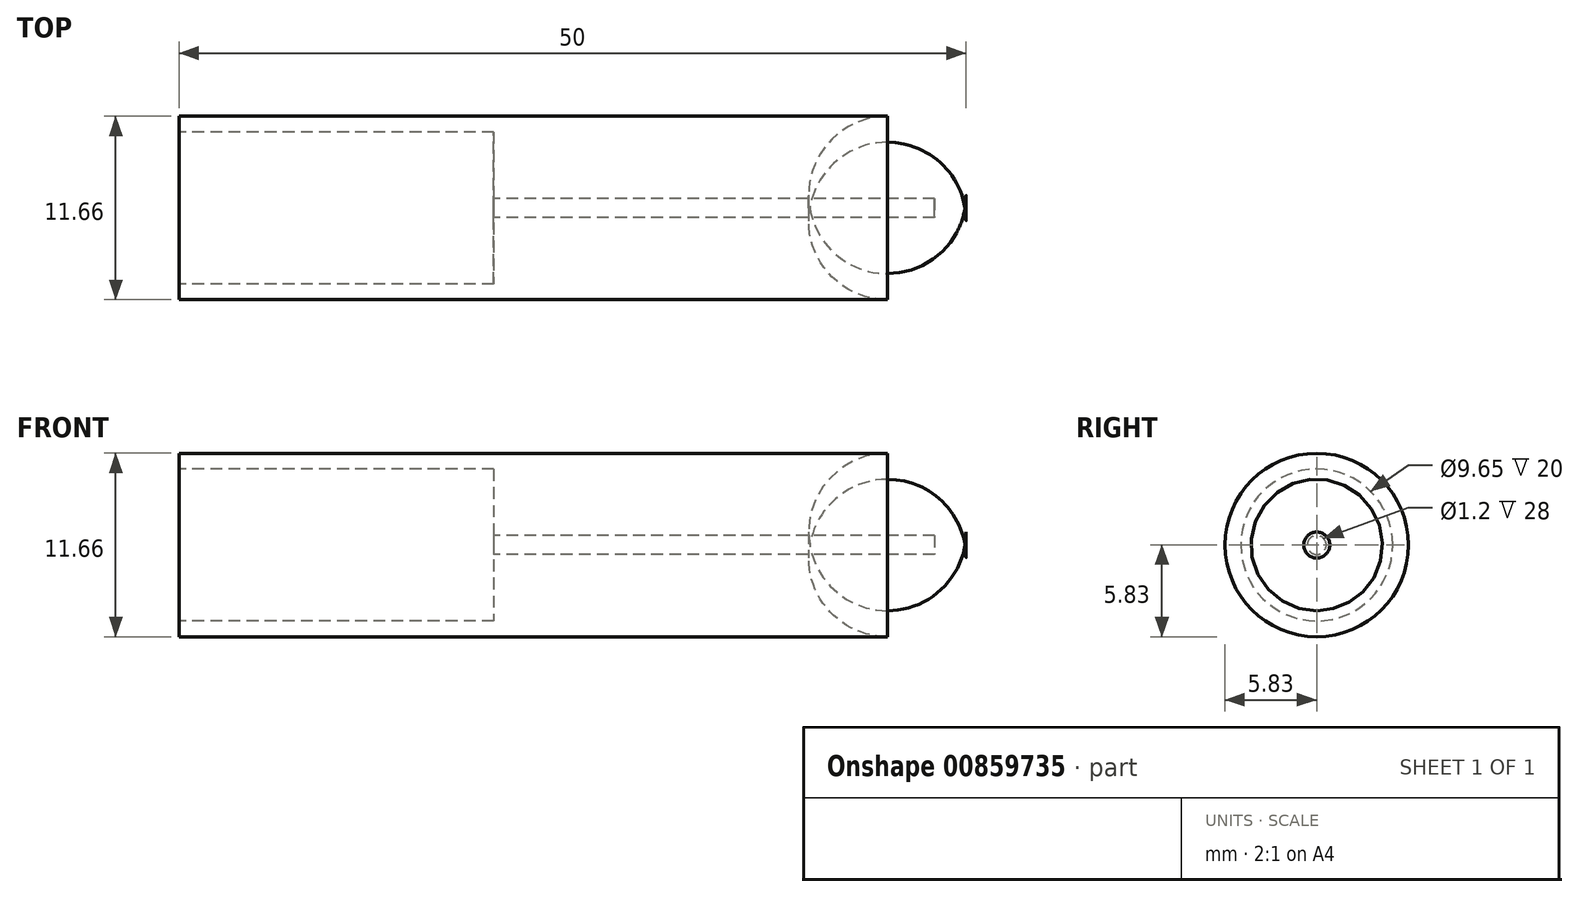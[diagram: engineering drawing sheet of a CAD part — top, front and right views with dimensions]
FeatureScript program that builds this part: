
annotation { "Feature Type Name" : "Feature", "Feature Type Description" : "" }
export const myFeature = defineFeature(function(context is Context, id is Id, definition is map)
    precondition{}
    {
        {
            var Q0;
            Q0=qCreatedBy(makeId("Front.planeOp"),FACE);
            var sketch = newSketch(context, id + "F0", { "sketchPlane" : qUnion([Q0])});
            skLineSegment(sketch, "E0", {"start": v(-11.62, 5.82) * mm, "end": v(-11.62, 4.83) * mm});
            skLineSegment(sketch, "E1", {"start": v(-11.62, 4.83) * mm, "end": v(8.38, 4.83) * mm});
            skLineSegment(sketch, "E2", {"start": v(8.38, 4.83) * mm, "end": v(8.38, 0.6) * mm});
            skLineSegment(sketch, "E3", {"start": v(8.38, 0.6) * mm, "end": v(36.38, 0.6) * mm});
            skLineSegment(sketch, "E4", {"start": v(38.38, 5.83) * mm, "end": v(-11.62, 5.82) * mm});
            skPoint(sketch, "E5", {"position": v(36.38, 0) * mm});
            skPoint(sketch, "E6", {"position": v(38.38, 0) * mm});
            skLineSegment(sketch, "E7", {"start": v(36.38, 0.6) * mm, "end": v(36.38, 0) * mm});
            skLineSegment(sketch, "E8", {"start": v(38.38, 0) * mm, "end": v(38.38, 5.83) * mm});
            skLineSegment(sketch, "E9", {"start": v(36.38, 0) * mm, "end": v(38.38, 0) * mm});
            skLineSegment(sketch, "E10", {"start": v(-25.87, 0) * mm, "end": v(66.18, 0) * mm, "construction": true});
            skSolve(sketch);
        }
        {
            var Q0;
            Q0 = qSketchRegion(id + "F0", true);
            var Q1;
            Q1=sQuery(id+"F0.wireOp",EDGE,"E10");
            revolve(context, id + "F1", {"surfaceOperationType" : NewSurfaceOperationType.NEW, "entities" : qUnion([Q0]), "axis" : qUnion([Q1]), "revolveType" : RevolveType.FULL});
        }
        {
            var Q0;
            Q0=makeQuery(id+"F1.opRevolve","SWEPT_EDGE",EDGE,{"disambiguationData":[OSD([sQuery(id+"F0.wireOp",EDGE,"E4"),sQuery(id+"F0.wireOp",EDGE,"E8")])]});
            fillet(context, id + "F2", {"entities" : qUnion([Q0]), "radius" : 5 * mm, "tangentPropagation" : true, "allowEdgeOverflow" : false});
        }
    });
